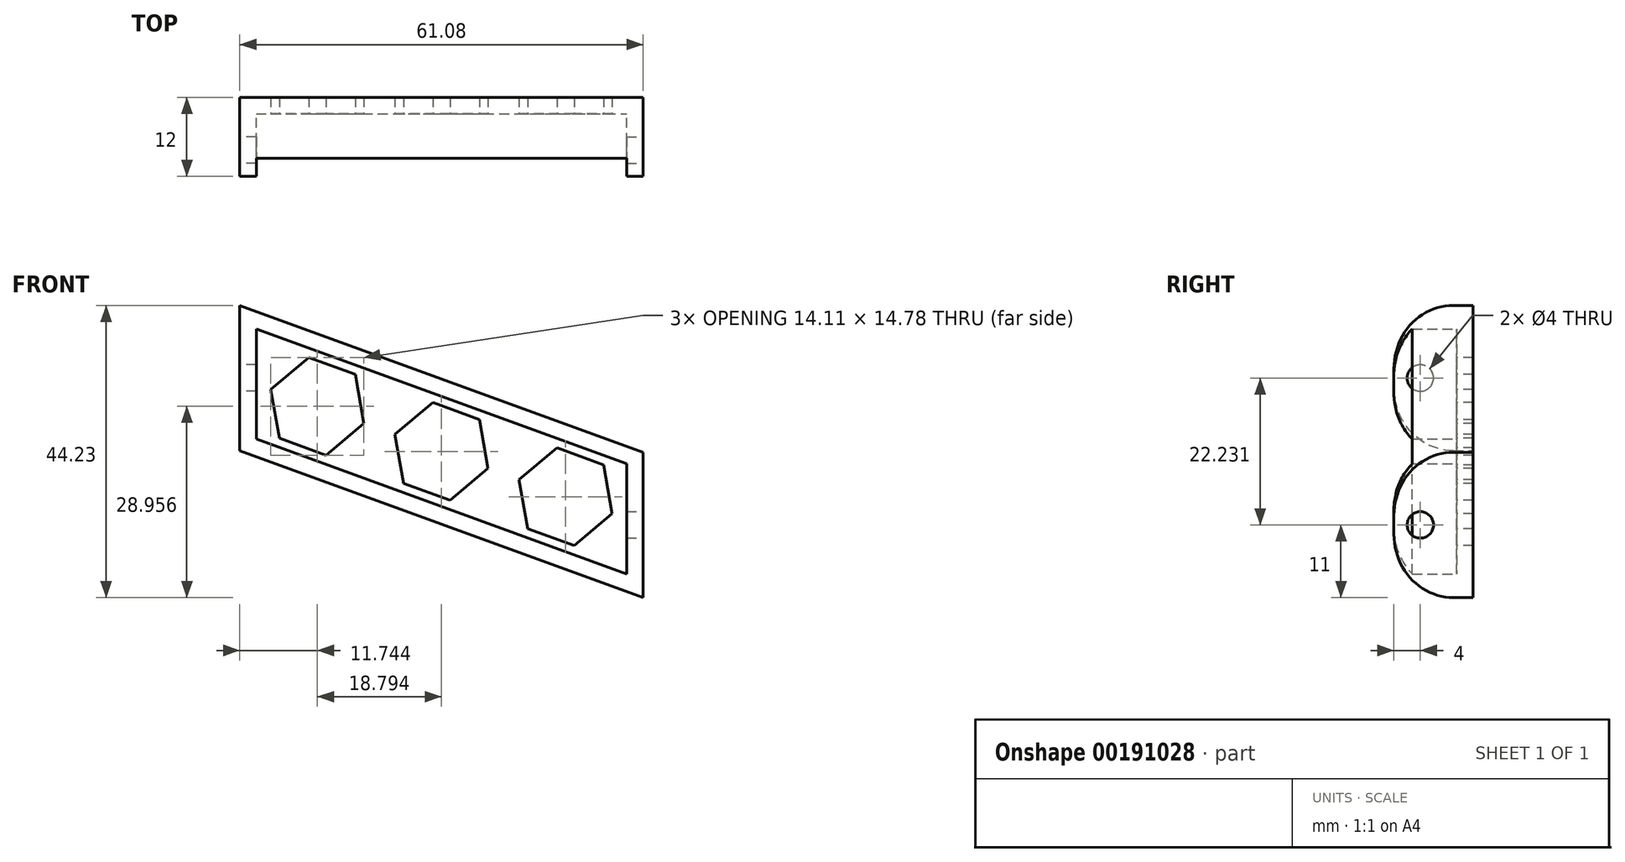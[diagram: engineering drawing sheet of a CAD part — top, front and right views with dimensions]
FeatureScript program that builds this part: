
annotation { "Feature Type Name" : "Feature", "Feature Type Description" : "" }
export const myFeature = defineFeature(function(context is Context, id is Id, definition is map)
    precondition{}
    {
        {
            var Q0;
            Q0=qCreatedBy(makeId("Front.planeOp"),FACE);
            var sketch = newSketch(context, id + "F0", { "sketchPlane" : qUnion([Q0])});
            skLineSegment(sketch, "E0", {"start": v(-21.6, 22.23) * mm, "end": v(39.49, 0) * mm});
            skLineSegment(sketch, "E1", {"start": v(39.49, 0) * mm, "end": v(39.49, -22) * mm});
            skLineSegment(sketch, "E2", {"start": v(39.49, -22) * mm, "end": v(-21.6, 0.23) * mm});
            skLineSegment(sketch, "E3", {"start": v(-21.6, 0.23) * mm, "end": v(-21.6, 22.23) * mm});
            skLineSegment(sketch, "E4", {"start": v(-37.67, -46.26) * mm, "end": v(59.8, -46.26) * mm, "construction": true});
            skLineSegment(sketch, "E5", {"start": v(77.46, 10.71) * mm, "end": v(77.46, -42.73) * mm, "construction": true});
            skSolve(sketch);
        }
        {
            var Q0;
            Q0=makeQuery(id+"F0.imprint","IMPRINT",FACE,{"disambiguationData":[TD([[makeQuery(id+"F0.imprint","IMPRINT",EDGE,{"derivedFrom":sQuery(id+"F0.wireOp",EDGE,"E0")}),-1.0]])]});
            extrude(context, id + "F1", {"entities" : qUnion([Q0]), "depth" : 12 * mm});
        }
        {
            var Q0;
            Q0=makeQuery(id+"F1.opExtrude","CAP_FACE",FACE,{"disambiguationData":[OSD([sQuery(id+"F0.wireOp",EDGE,"E0"),sQuery(id+"F0.wireOp",EDGE,"E1"),sQuery(id+"F0.wireOp",EDGE,"E2"),sQuery(id+"F0.wireOp",EDGE,"E3")])],"isStart":false});
            shell(context, id + "F2", {"entities" : qUnion([Q0]), "thickness" : 2.5 * mm});
        }
        {
            var Q0;
            Q0=makeQuery(id+"F1.opExtrude","SWEPT_FACE",FACE,{"disambiguationData":[OSD([sQuery(id+"F0.wireOp",EDGE,"E3")])]});
            var sketch = newSketch(context, id + "F3", { "sketchPlane" : qUnion([Q0])});
            skPoint(sketch, "E6", {"position": v(8, 11.23) * mm});
            skLineSegment(sketch, "E7", {"start": v(0, 11.23) * mm, "end": v(12, 11.23) * mm, "construction": true});
            skLineSegment(sketch, "E8.bottom", {"start": v(0, 22.23) * mm, "end": v(12, 22.23) * mm});
            skLineSegment(sketch, "E8.top", {"start": v(0, 0.23) * mm, "end": v(12, 0.23) * mm});
            skLineSegment(sketch, "E8.left", {"start": v(0, 22.23) * mm, "end": v(0, 0.23) * mm});
            skLineSegment(sketch, "E8.right", {"start": v(12, 22.23) * mm, "end": v(12, 0.23) * mm});
            skSolve(sketch);
        }
        {
            var Q0;
            Q0=sQuery(id+"F3.wireOp",VERTEX,"E6");
            var Q1;
            Q1=makeQuery(id+"F1.opExtrude","SWEPT_BODY",BODY,{"disambiguationData":[OSD([sQuery(id+"F0.wireOp",EDGE,"E0"),sQuery(id+"F0.wireOp",EDGE,"E1"),sQuery(id+"F0.wireOp",EDGE,"E2"),sQuery(id+"F0.wireOp",EDGE,"E3")])]});
            hole(context, id + "F4", {"style" : HoleStyle.SIMPLE, "endStyle" : HoleEndStyle.BLIND, "holeDiameter" : 4 * mm, "holeDepth" : 6 * mm, "locations" : qUnion([Q0]), "scope" : qUnion([Q1])});
        }
        {
            var Q0;
            Q0=makeQuery(id+"F1.opExtrude","SWEPT_FACE",FACE,{"disambiguationData":[OSD([sQuery(id+"F0.wireOp",EDGE,"E1")])]});
            var sketch = newSketch(context, id + "F5", { "sketchPlane" : qUnion([Q0])});
            skPoint(sketch, "E9", {"position": v(-8, -11) * mm});
            skLineSegment(sketch, "E10", {"start": v(-12, -11) * mm, "end": v(0, -11) * mm, "construction": true});
            skSolve(sketch);
        }
        {
            var Q0;
            Q0=sQuery(id+"F5.wireOp",VERTEX,"E9");
            var Q1;
            Q1=makeQuery(id+"F1.opExtrude","SWEPT_BODY",BODY,{"disambiguationData":[OSD([sQuery(id+"F0.wireOp",EDGE,"E0"),sQuery(id+"F0.wireOp",EDGE,"E1"),sQuery(id+"F0.wireOp",EDGE,"E2"),sQuery(id+"F0.wireOp",EDGE,"E3")])]});
            hole(context, id + "F6", {"style" : HoleStyle.SIMPLE, "endStyle" : HoleEndStyle.BLIND, "holeDiameter" : 4 * mm, "holeDepth" : 6 * mm, "locations" : qUnion([Q0]), "scope" : qUnion([Q1])});
        }
        {
            var Q0;
            Q0=makeQuery(id+"F1.opExtrude","CAP_EDGE",EDGE,{"disambiguationData":[OSD([sQuery(id+"F0.wireOp",EDGE,"E0")])],"isStart":false});
            var Q1;
            Q1=makeQuery(id+"F1.opExtrude","CAP_EDGE",EDGE,{"disambiguationData":[OSD([sQuery(id+"F0.wireOp",EDGE,"E2")])],"isStart":false});
            fillet(context, id + "F7", {"entities" : qUnion([Q0, Q1]), "radius" : 9 * mm, "tangentPropagation" : true, "allowEdgeOverflow" : false});
        }
        {
            var Q0;
            Q0=makeQuery(id+"F2.opShell","OFFSET_FACE",FACE,{"disambiguationData":[OSD([sQuery(id+"F0.wireOp",EDGE,"E0"),sQuery(id+"F0.wireOp",EDGE,"E1"),sQuery(id+"F0.wireOp",EDGE,"E2"),sQuery(id+"F0.wireOp",EDGE,"E3")])]});
            var sketch = newSketch(context, id + "F8", { "sketchPlane" : qUnion([Q0])});
            skCircle(sketch, "E11.cCircle", {"center": v(-9.85, 6.96) * mm, "radius": 6.5 * mm, "construction": true});
            skLineSegment(sketch, "E11.0", {"start": v(-2.8, 4.39) * mm, "end": v(-8.54, -0.44) * mm});
            skLineSegment(sketch, "E11.1", {"start": v(-8.54, -0.44) * mm, "end": v(-15.6, 2.13) * mm});
            skLineSegment(sketch, "E11.2", {"start": v(-15.6, 2.13) * mm, "end": v(-16.9, 9.52) * mm});
            skLineSegment(sketch, "E11.3", {"start": v(-16.9, 9.52) * mm, "end": v(-11.15, 14.35) * mm});
            skLineSegment(sketch, "E11.4", {"start": v(-11.15, 14.35) * mm, "end": v(-4.1, 11.78) * mm});
            skLineSegment(sketch, "E11.5", {"start": v(-4.1, 11.78) * mm, "end": v(-2.8, 4.39) * mm});
            skPoint(sketch, "E11.0.midPoint", {"position": v(-5.67, 1.98) * mm});
            skLineSegment(sketch, "E12", {"start": v(8.95, 0.12) * mm, "end": v(-19.1, 10.32) * mm, "construction": true});
            skCircle(sketch, "E13.cCircle", {"center": v(8.95, 0.12) * mm, "radius": 6.5 * mm, "construction": true});
            skLineSegment(sketch, "E13.0", {"start": v(16, -2.45) * mm, "end": v(10.25, -7.28) * mm});
            skLineSegment(sketch, "E13.1", {"start": v(10.25, -7.28) * mm, "end": v(3.2, -4.7) * mm});
            skLineSegment(sketch, "E13.2", {"start": v(3.2, -4.7) * mm, "end": v(1.9, 2.68) * mm});
            skLineSegment(sketch, "E13.3", {"start": v(1.9, 2.68) * mm, "end": v(7.64, 7.5) * mm});
            skLineSegment(sketch, "E13.4", {"start": v(7.64, 7.5) * mm, "end": v(14.7, 4.94) * mm});
            skLineSegment(sketch, "E13.5", {"start": v(14.7, 4.94) * mm, "end": v(16, -2.45) * mm});
            skCircle(sketch, "E14.cCircle", {"center": v(27.74, -6.72) * mm, "radius": 6.5 * mm, "construction": true});
            skLineSegment(sketch, "E14.0", {"start": v(34.8, -9.3) * mm, "end": v(29.04, -14.12) * mm});
            skLineSegment(sketch, "E14.1", {"start": v(29.04, -14.12) * mm, "end": v(22, -11.55) * mm});
            skLineSegment(sketch, "E14.2", {"start": v(22, -11.55) * mm, "end": v(20.69, -4.16) * mm});
            skLineSegment(sketch, "E14.3", {"start": v(20.69, -4.16) * mm, "end": v(26.44, 0.67) * mm});
            skLineSegment(sketch, "E14.4", {"start": v(26.44, 0.67) * mm, "end": v(33.5, -1.9) * mm});
            skLineSegment(sketch, "E14.5", {"start": v(33.5, -1.9) * mm, "end": v(34.8, -9.3) * mm});
            skLineSegment(sketch, "E15", {"start": v(8.95, 0.12) * mm, "end": v(36.99, -10.1) * mm, "construction": true});
            skLineSegment(sketch, "E16", {"start": v(8.95, 8.46) * mm, "end": v(8.95, -8.22) * mm, "construction": true});
            skSolve(sketch);
        }
        {
            var Q0;
            Q0=makeQuery(id+"F8.imprint","IMPRINT",FACE,{"disambiguationData":[TD([[makeQuery(id+"F8.imprint","IMPRINT",EDGE,{"derivedFrom":sQuery(id+"F8.wireOp",EDGE,"E11.0")}),-1.0]])]});
            var Q1;
            Q1=makeQuery(id+"F8.imprint","IMPRINT",FACE,{"disambiguationData":[TD([[makeQuery(id+"F8.imprint","IMPRINT",EDGE,{"derivedFrom":sQuery(id+"F8.wireOp",EDGE,"E13.0")}),-1.0]])]});
            var Q2;
            Q2=makeQuery(id+"F8.imprint","IMPRINT",FACE,{"disambiguationData":[TD([[makeQuery(id+"F8.imprint","IMPRINT",EDGE,{"derivedFrom":sQuery(id+"F8.wireOp",EDGE,"E14.0")}),-1.0]])]});
            extrude(context, id + "F9", {"entities" : qUnion([Q0, Q1, Q2]), "operationType" : NewBodyOperationType.REMOVE, "oppositeDirection" : true, "depth" : 25 * mm});
        }
    });
